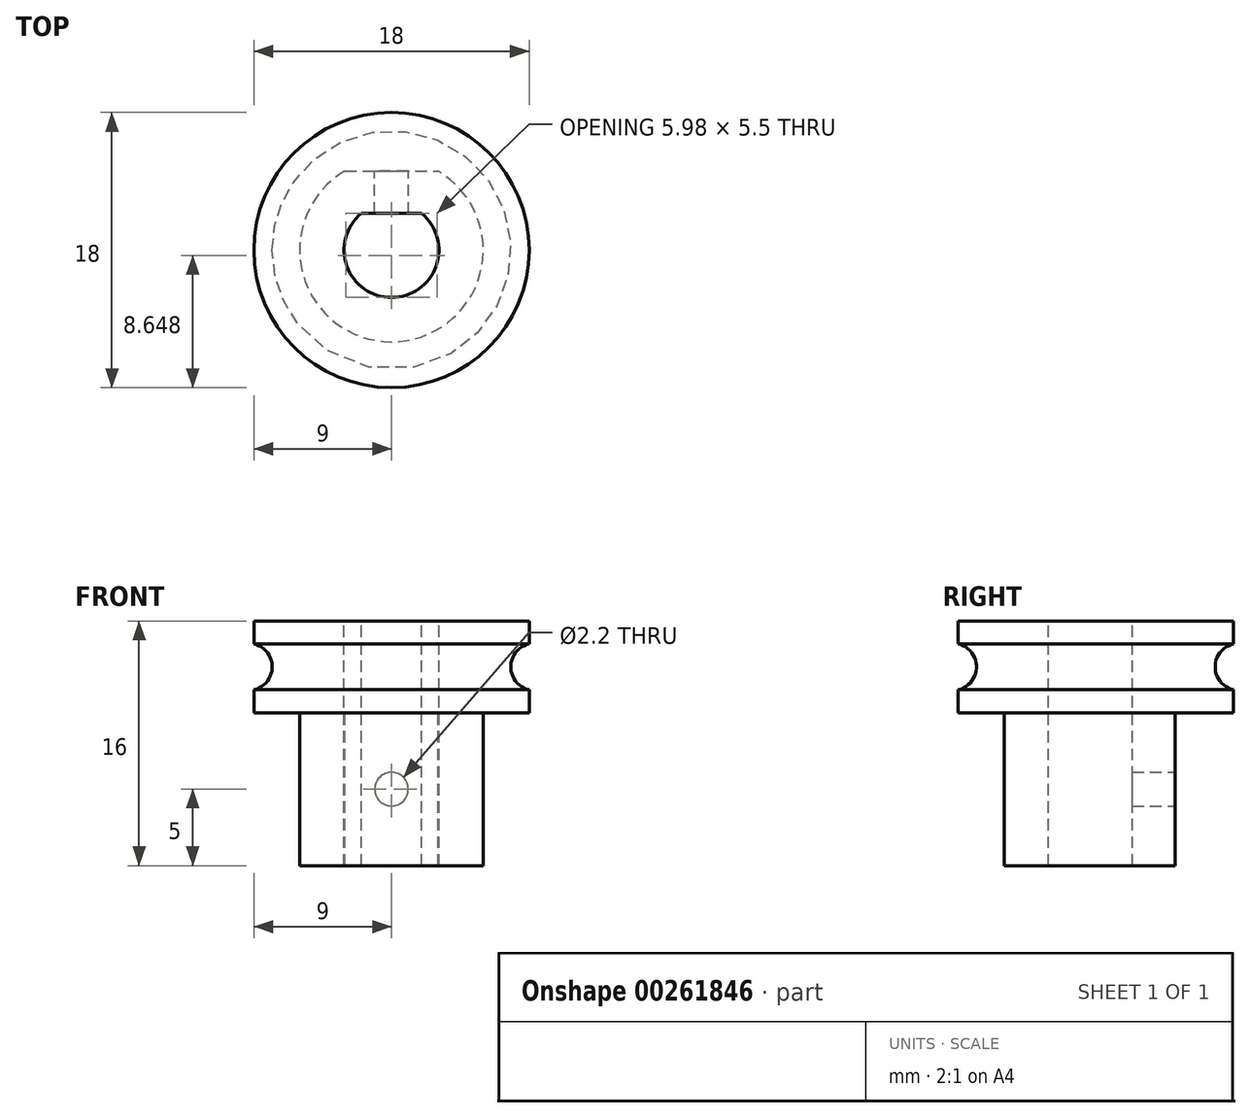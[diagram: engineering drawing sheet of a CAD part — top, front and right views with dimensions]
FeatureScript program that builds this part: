
annotation { "Feature Type Name" : "Feature", "Feature Type Description" : "" }
export const myFeature = defineFeature(function(context is Context, id is Id, definition is map)
    precondition{}
    {
        {
            var Q0;
            Q0=qCreatedBy(makeId("Front.planeOp"),FACE);
            var sketch = newSketch(context, id + "F0", { "sketchPlane" : qUnion([Q0])});
            skLineSegment(sketch, "E0", {"start": v(0, 0) * mm, "end": v(-9, 0) * mm});
            skLineSegment(sketch, "E1", {"start": v(-9, 0) * mm, "end": v(-9, 1.5) * mm});
            skLineSegment(sketch, "E2", {"start": v(0, 3) * mm, "end": v(-18.74, 3) * mm, "construction": true});
            skLineSegment(sketch, "E3.MirrorCS", {"start": v(-9, 6) * mm, "end": v(-9, 4.5) * mm});
            skLineSegment(sketch, "E4.MirrorCS", {"start": v(0, 6) * mm, "end": v(-9, 6) * mm});
            skArc(sketch, "E5", {"start": v(-9, 1.5) * mm, "mid": v(-7.8, 3) * mm, "end": v(-9, 4.5) * mm});
            skLineSegment(sketch, "E6", {"start": v(0, 0) * mm, "end": v(0, 6) * mm});
            skLineSegment(sketch, "E7", {"start": v(-7.8, 6) * mm, "end": v(-7.8, 0) * mm, "construction": true});
            skSolve(sketch);
        }
        {
            var Q0;
            Q0=qSketchRegion(id+"F0",true);
            var Q1;
            Q1=sQuery(id+"F0.wireOp",EDGE,"E6");
            revolve(context, id + "F1", {"entities" : qUnion([Q0]), "axis" : qUnion([Q1]), "revolveType" : RevolveType.FULL});
        }
        {
            var Q0;
            Q0=makeQuery(id+"F1.opRevolve","SWEPT_FACE",FACE,{"disambiguationData":[OSD([sQuery(id+"F0.wireOp",EDGE,"E4.MirrorCS")])]});
            var sketch = newSketch(context, id + "F2", { "sketchPlane" : qUnion([Q0])});
            skCircle(sketch, "E8", {"center": v(0, 0) * mm, "radius": 3.1 * mm, "construction": true});
            skLineSegment(sketch, "E9", {"start": v(-1.97, 2.4) * mm, "end": v(1.97, 2.4) * mm});
            skArc(sketch, "E10", {"start": v(-1.97, 2.4) * mm, "mid": v(0, -3.1) * mm, "end": v(1.97, 2.4) * mm});
            skSolve(sketch);
        }
        {
            var Q0;
            Q0=qCreatedBy(makeId("Top.planeOp"),FACE);
            var sketch = newSketch(context, id + "F3", { "sketchPlane" : qUnion([Q0])});
            skCircle(sketch, "E11", {"center": v(0, 0) * mm, "radius": 6 * mm, "construction": true});
            skLineSegment(sketch, "E12", {"start": v(-3.04, 5.18) * mm, "end": v(3.04, 5.18) * mm});
            skArc(sketch, "E13", {"start": v(-3.04, 5.18) * mm, "mid": v(0, -6) * mm, "end": v(3.04, 5.18) * mm});
            skSolve(sketch);
        }
        {
            var Q0;
            Q0=makeQuery(id+"F3.imprint","IMPRINT",FACE,{"disambiguationData":[TD([[makeQuery(id+"F3.imprint","IMPRINT",EDGE,{"derivedFrom":sQuery(id+"F3.wireOp",EDGE,"E12")}),-1.0]])]});
            extrude(context, id + "F4", {"entities" : qUnion([Q0]), "operationType" : NewBodyOperationType.ADD, "oppositeDirection" : true, "depth" : 10 * mm});
        }
        {
            var Q0;
            Q0=makeQuery(id+"F2.imprint","IMPRINT",FACE,{"disambiguationData":[TD([[makeQuery(id+"F2.imprint","IMPRINT",EDGE,{"derivedFrom":sQuery(id+"F2.wireOp",EDGE,"E9")}),-1.0]])]});
            extrude(context, id + "F5", {"entities" : qUnion([Q0]), "operationType" : NewBodyOperationType.REMOVE, "endBound" : BoundingType.THROUGH_ALL, "oppositeDirection" : true, "depth" : 25 * mm});
        }
        {
            var Q0;
            Q0=makeQuery(id+"F4.opExtrude","SWEPT_FACE",FACE,{"disambiguationData":[OSD([sQuery(id+"F3.wireOp",EDGE,"E12")])]});
            var sketch = newSketch(context, id + "F6", { "sketchPlane" : qUnion([Q0])});
            skLineSegment(sketch, "E14", {"start": v(3.04, -10) * mm, "end": v(-3.04, 0) * mm, "construction": true});
            skLineSegment(sketch, "E15", {"start": v(-3.04, 0) * mm, "end": v(3.04, 0) * mm, "construction": true});
            skLineSegment(sketch, "E16", {"start": v(3.04, 0) * mm, "end": v(-3.04, -10) * mm, "construction": true});
            skPoint(sketch, "E17", {"position": v(0, -5) * mm});
            skSolve(sketch);
        }
        {
            var Q0;
            Q0=sQuery(id+"F6.wireOp",VERTEX,"E17");
            var Q1;
            Q1=makeQuery(id+"F1.opRevolve","SWEPT_BODY",BODY,{"disambiguationData":[OSD([sQuery(id+"F0.wireOp",EDGE,"E0"),sQuery(id+"F0.wireOp",EDGE,"E1"),sQuery(id+"F0.wireOp",EDGE,"E3.MirrorCS"),sQuery(id+"F0.wireOp",EDGE,"E4.MirrorCS"),sQuery(id+"F0.wireOp",EDGE,"E5"),sQuery(id+"F0.wireOp",EDGE,"E6")])]});
            hole(context, id + "F7", {"style" : HoleStyle.SIMPLE, "endStyle" : HoleEndStyle.BLIND, "holeDiameter" : 2.2 * mm, "holeDepth" : 4 * mm, "tappedDepth" : 12 * mm, "tapClearance" : 3, "locations" : qUnion([Q0]), "scope" : qUnion([Q1])});
        }
    });
